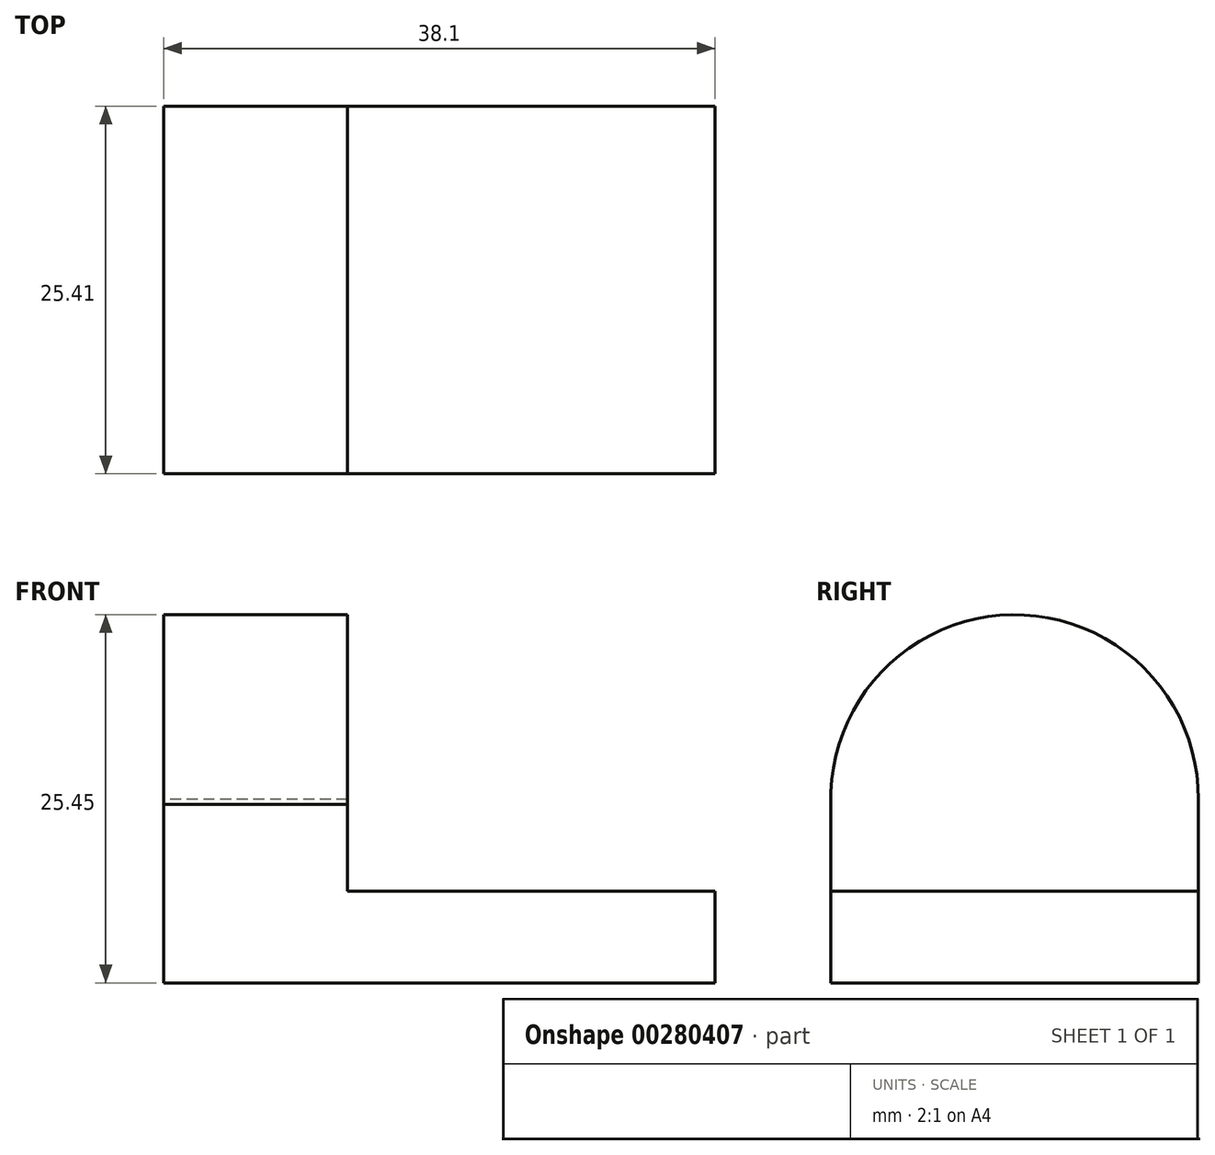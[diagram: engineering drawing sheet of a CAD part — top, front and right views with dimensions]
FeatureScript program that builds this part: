
annotation { "Feature Type Name" : "Feature", "Feature Type Description" : "" }
export const myFeature = defineFeature(function(context is Context, id is Id, definition is map)
    precondition{}
    {
        {
            var Q0;
            Q0=qCreatedBy(makeId("Front.planeOp"),FACE);
            var sketch = newSketch(context, id + "F0", { "sketchPlane" : qUnion([Q0])});
            skLineSegment(sketch, "E0", {"start": v(0, 0) * mm, "end": v(0, 6.35) * mm});
            skLineSegment(sketch, "E1", {"start": v(0, 6.35) * mm, "end": v(38.1, 6.35) * mm});
            skLineSegment(sketch, "E2", {"start": v(38.1, 6.35) * mm, "end": v(38.1, 0) * mm});
            skLineSegment(sketch, "E3", {"start": v(38.1, 0) * mm, "end": v(0, 0) * mm});
            skSolve(sketch);
        }
        {
            var Q0;
            Q0 = qSketchRegion(id + "F0", true);
            extrude(context, id + "F1", {"entities" : qUnion([Q0]), "depth" : 25.4 * mm});
        }
        {
            var Q0;
            Q0=qCreatedBy(makeId("Right.planeOp"),FACE);
            var sketch = newSketch(context, id + "F2", { "sketchPlane" : qUnion([Q0])});
            skLineSegment(sketch, "E4", {"start": v(0, 6.35) * mm, "end": v(0, 12.7) * mm});
            skLineSegment(sketch, "E5", {"start": v(0, 12.7) * mm, "end": v(-25.4, 12.7) * mm});
            skLineSegment(sketch, "E6", {"start": v(-25.4, 12.7) * mm, "end": v(-25.4, 6.35) * mm});
            skLineSegment(sketch, "E7", {"start": v(-25.4, 6.35) * mm, "end": v(0, 6.35) * mm});
            skSolve(sketch);
        }
        {
            var Q0;
            Q0 = qSketchRegion(id + "F2", true);
            extrude(context, id + "F3", {"entities" : qUnion([Q0]), "operationType" : NewBodyOperationType.ADD, "depth" : 12.7 * mm});
        }
        {
            var Q0;
            Q0=qCreatedBy(makeId("Right.planeOp"),FACE);
            var sketch = newSketch(context, id + "F4", { "sketchPlane" : qUnion([Q0])});
            skCircle(sketch, "E8", {"center": v(-12.7, 12.75) * mm, "radius": 12.7 * mm});
            skSolve(sketch);
        }
        {
            var Q0;
            Q0 = qSketchRegion(id + "F4", true);
            extrude(context, id + "F5", {"entities" : qUnion([Q0]), "operationType" : NewBodyOperationType.ADD, "depth" : 12.7 * mm});
        }
    });
